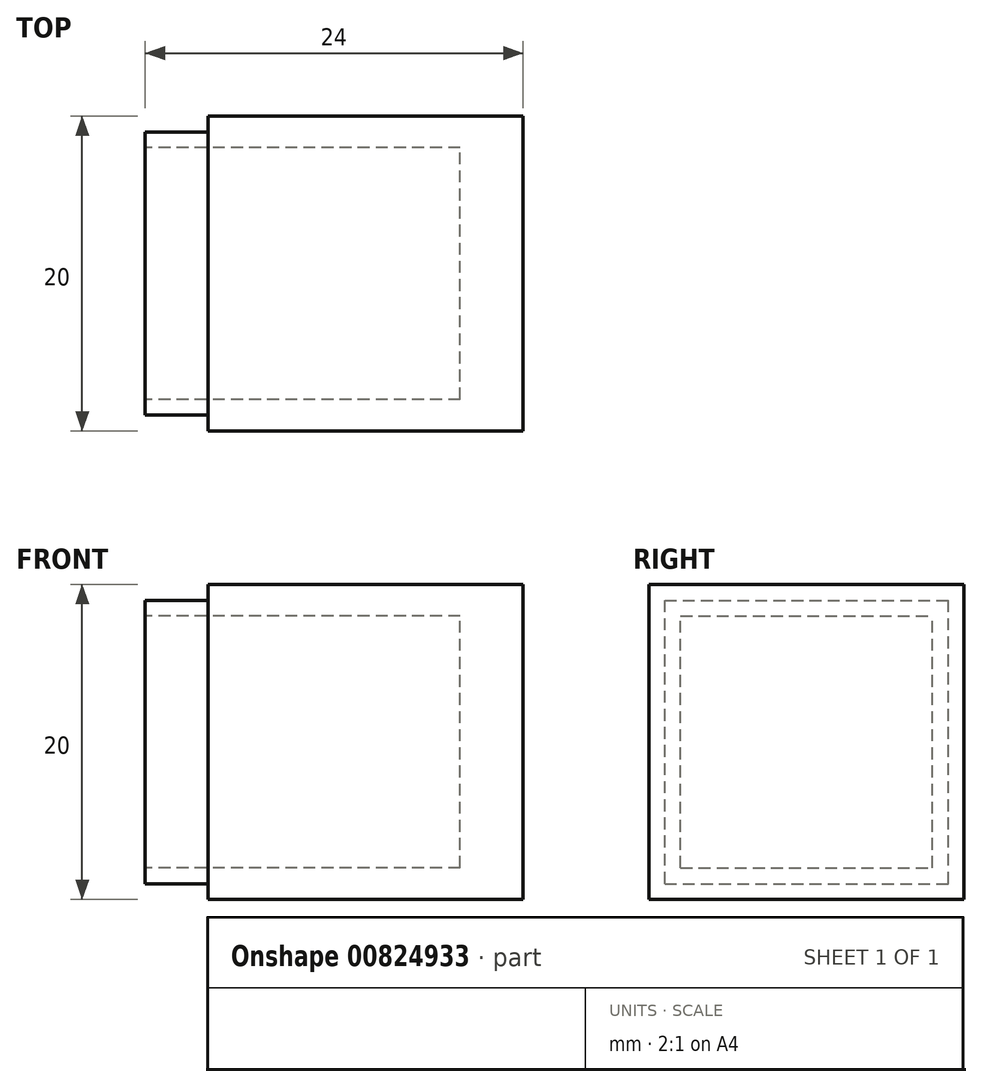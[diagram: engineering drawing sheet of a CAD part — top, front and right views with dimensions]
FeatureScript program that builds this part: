
annotation { "Feature Type Name" : "Feature", "Feature Type Description" : "" }
export const myFeature = defineFeature(function(context is Context, id is Id, definition is map)
    precondition{}
    {
        {
            var Q0;
            Q0=qCreatedBy(makeId("Right.planeOp"),FACE);
            var sketch = newSketch(context, id + "F0", { "sketchPlane" : qUnion([Q0])});
            skLineSegment(sketch, "E0.bottom", {"start": v(-10, -10) * mm, "end": v(10, -10) * mm});
            skLineSegment(sketch, "E0.top", {"start": v(-10, 10) * mm, "end": v(10, 10) * mm});
            skLineSegment(sketch, "E0.left", {"start": v(-10, -10) * mm, "end": v(-10, 10) * mm});
            skLineSegment(sketch, "E0.right", {"start": v(10, -10) * mm, "end": v(10, 10) * mm});
            skPoint(sketch, "E0.middle", {"position": v(0, 0) * mm});
            skSolve(sketch);
        }
        {
            var Q0;
            Q0 = qSketchRegion(id + "F0", true);
            extrude(context, id + "F1", {"entities" : qUnion([Q0]), "depth" : 20 * mm, "offsetDistance" : 25 * mm});
        }
        {
            var Q0;
            Q0=makeQuery(id+"F1.opExtrude","CAP_FACE",FACE,{"disambiguationData":[OSD([sQuery(id+"F0.wireOp",EDGE,"E0.bottom"),sQuery(id+"F0.wireOp",EDGE,"E0.top"),sQuery(id+"F0.wireOp",EDGE,"E0.left"),sQuery(id+"F0.wireOp",EDGE,"E0.right")])],"isStart":true});
            var sketch = newSketch(context, id + "F2", { "sketchPlane" : qUnion([Q0])});
            skLineSegment(sketch, "E1.bottom", {"start": v(8, -8) * mm, "end": v(-8, -8) * mm});
            skLineSegment(sketch, "E1.top", {"start": v(8, 8) * mm, "end": v(-8, 8) * mm});
            skLineSegment(sketch, "E1.left", {"start": v(8, -8) * mm, "end": v(8, 8) * mm});
            skLineSegment(sketch, "E1.right", {"start": v(-8, -8) * mm, "end": v(-8, 8) * mm});
            skPoint(sketch, "E1.middle", {"position": v(0, 0) * mm});
            skSolve(sketch);
        }
        {
            var Q0;
            Q0 = qSketchRegion(id + "F2", true);
            extrude(context, id + "F3", {"entities" : qUnion([Q0]), "operationType" : NewBodyOperationType.REMOVE, "oppositeDirection" : true, "depth" : 16 * mm, "offsetDistance" : 25 * mm});
        }
        {
            var Q0;
            Q0=makeQuery(id+"F1.opExtrude","CAP_FACE",FACE,{"disambiguationData":[OSD([sQuery(id+"F0.wireOp",EDGE,"E0.bottom"),sQuery(id+"F0.wireOp",EDGE,"E0.top"),sQuery(id+"F0.wireOp",EDGE,"E0.left"),sQuery(id+"F0.wireOp",EDGE,"E0.right")])],"isStart":true});
            var sketch = newSketch(context, id + "F4", { "sketchPlane" : qUnion([Q0])});
            skLineSegment(sketch, "E2.bottom", {"start": v(9, -9) * mm, "end": v(-9, -9) * mm});
            skLineSegment(sketch, "E2.top", {"start": v(9, 9) * mm, "end": v(-9, 9) * mm});
            skLineSegment(sketch, "E2.left", {"start": v(9, -9) * mm, "end": v(9, 9) * mm});
            skLineSegment(sketch, "E2.right", {"start": v(-9, -9) * mm, "end": v(-9, 9) * mm});
            skPoint(sketch, "E2.middle", {"position": v(0, 0) * mm});
            skSolve(sketch);
        }
        {
            var Q0;
            Q0=makeQuery(id+"F4.imprint","IMPRINT",FACE,{"disambiguationData":[TD([[makeQuery(id+"F4.imprint","IMPRINT",EDGE,{"derivedFrom":sQuery(id+"F4.wireOp",EDGE,"E2.bottom")}),-1.0]])]});
            extrude(context, id + "F5", {"entities" : qUnion([Q0]), "operationType" : NewBodyOperationType.ADD, "depth" : 4 * mm, "offsetDistance" : 25 * mm});
        }
    });
